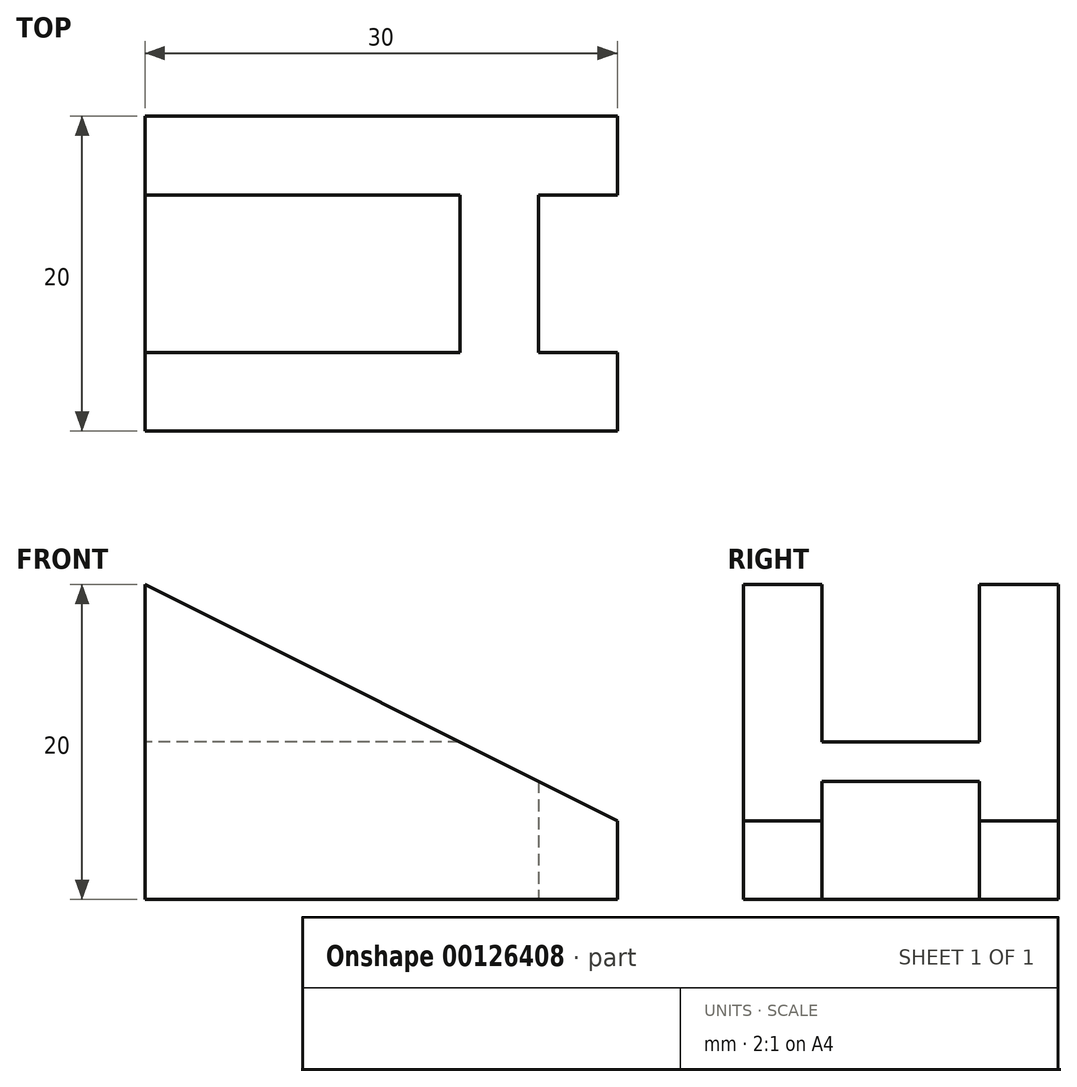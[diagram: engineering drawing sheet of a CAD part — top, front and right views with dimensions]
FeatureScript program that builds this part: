
annotation { "Feature Type Name" : "Feature", "Feature Type Description" : "" }
export const myFeature = defineFeature(function(context is Context, id is Id, definition is map)
    precondition{}
    {
        {
            var Q0;
            Q0=qCreatedBy(makeId("Front.planeOp"),FACE);
            var sketch = newSketch(context, id + "F0", { "sketchPlane" : qUnion([Q0])});
            skLineSegment(sketch, "E0", {"start": v(0, 0) * mm, "end": v(0, 20) * mm});
            skLineSegment(sketch, "E1", {"start": v(0, 20) * mm, "end": v(30, 5) * mm});
            skLineSegment(sketch, "E2", {"start": v(30, 5) * mm, "end": v(30, 0) * mm});
            skLineSegment(sketch, "E3", {"start": v(30, 0) * mm, "end": v(0, 0) * mm});
            skSolve(sketch);
        }
        {
            var Q0;
            Q0 = qSketchRegion(id + "F0", true);
            extrude(context, id + "F1", {"entities" : qUnion([Q0]), "depth" : 20 * mm});
        }
        {
            var Q0;
            Q0=qCreatedBy(makeId("Right.planeOp"),FACE);
            var sketch = newSketch(context, id + "F2", { "sketchPlane" : qUnion([Q0])});
            skLineSegment(sketch, "E4", {"start": v(-15, 20) * mm, "end": v(-15, 10) * mm});
            skLineSegment(sketch, "E5", {"start": v(-15, 10) * mm, "end": v(-5, 10) * mm});
            skLineSegment(sketch, "E6", {"start": v(-5, 10) * mm, "end": v(-5, 20) * mm});
            skLineSegment(sketch, "E7.0", {"start": v(-20, 20) * mm, "end": v(0, 20) * mm});
            skSolve(sketch);
        }
        {
            var Q0;
            Q0 = qSketchRegion(id + "F2", true);
            extrude(context, id + "F3", {"entities" : qUnion([Q0]), "operationType" : NewBodyOperationType.REMOVE, "depth" : 25 * mm});
        }
        {
            var Q0;
            Q0=qCreatedBy(makeId("Top.planeOp"),FACE);
            var sketch = newSketch(context, id + "F4", { "sketchPlane" : qUnion([Q0])});
            skLineSegment(sketch, "E8", {"start": v(25, -15) * mm, "end": v(30, -15) * mm});
            skLineSegment(sketch, "E9", {"start": v(25, -15) * mm, "end": v(25, -5) * mm});
            skLineSegment(sketch, "E10", {"start": v(25, -5) * mm, "end": v(30, -5) * mm});
            skLineSegment(sketch, "E11.0", {"start": v(30, -20) * mm, "end": v(30, 0) * mm});
            skSolve(sketch);
        }
        {
            var Q0;
            Q0 = qSketchRegion(id + "F4", true);
            extrude(context, id + "F5", {"entities" : qUnion([Q0]), "operationType" : NewBodyOperationType.REMOVE, "depth" : 25 * mm});
        }
    });
